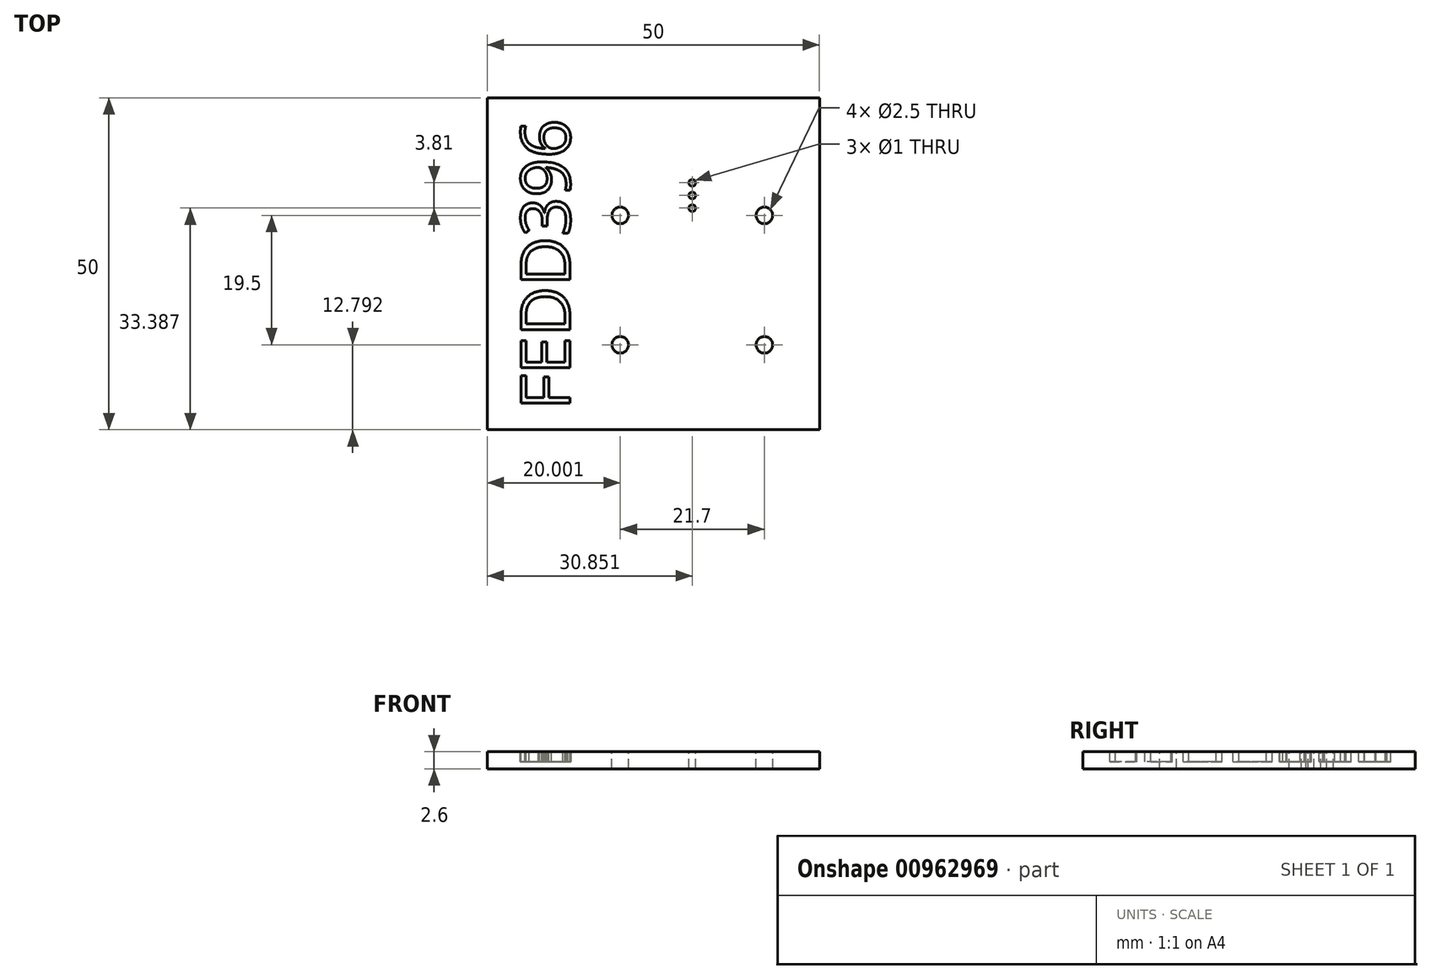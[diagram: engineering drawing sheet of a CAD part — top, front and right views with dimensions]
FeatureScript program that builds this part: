
annotation { "Feature Type Name" : "Feature", "Feature Type Description" : "" }
export const myFeature = defineFeature(function(context is Context, id is Id, definition is map)
    precondition{}
    {
        {
            var Q0;
            Q0=qCreatedBy(makeId("Top.planeOp"),FACE);
            var sketch = newSketch(context, id + "F0", { "sketchPlane" : qUnion([Q0])});
            skLineSegment(sketch, "E0.bottom", {"start": v(-43.16, 28.34) * mm, "end": v(6.84, 28.34) * mm});
            skLineSegment(sketch, "E0.top", {"start": v(-43.16, -21.66) * mm, "end": v(6.84, -21.66) * mm});
            skLineSegment(sketch, "E0.left", {"start": v(-43.16, 28.34) * mm, "end": v(-43.16, -21.66) * mm});
            skLineSegment(sketch, "E0.right", {"start": v(6.84, 28.34) * mm, "end": v(6.84, -21.66) * mm});
            skSolve(sketch);
        }
        {
            var Q0;
            Q0=makeQuery(id+"F0.imprint","IMPRINT",FACE,{"disambiguationData":[TD([[makeQuery(id+"F0.imprint","IMPRINT",EDGE,{"derivedFrom":sQuery(id+"F0.wireOp",EDGE,"E0.bottom")}),-1.0]])]});
            extrude(context, id + "F1", {"entities" : qUnion([Q0]), "depth" : 2.6 * mm, "offsetDistance" : 25 * mm});
        }
        {
            var Q0;
            Q0=makeQuery(id+"F1.opExtrude","CAP_FACE",FACE,{"disambiguationData":[OSD([sQuery(id+"F0.wireOp",EDGE,"E0.bottom"),sQuery(id+"F0.wireOp",EDGE,"E0.top"),sQuery(id+"F0.wireOp",EDGE,"E0.left"),sQuery(id+"F0.wireOp",EDGE,"E0.right")])],"isStart":false});
            var sketch = newSketch(context, id + "F2", { "sketchPlane" : qUnion([Q0])});
            skText(sketch, "E1", { "text": "FEDD396", "fontName": "OpenSans-Regular.ttf"});
            const initialGuessF2  = {"E1": [-0.03072, -0.01866, 0, 1, 0.00743]};
            skSetInitialGuess(sketch, initialGuessF2);
            skSolve(sketch);
        }
        {
            var Q0;
            Q0=qSketchRegion(id+"F2",true);
            extrude(context, id + "F3", {"entities" : qUnion([Q0]), "operationType" : NewBodyOperationType.REMOVE, "oppositeDirection" : true, "depth" : 1.5 * mm, "offsetDistance" : 25 * mm});
        }
        {
            var Q0;
            {var subQ0=sQuery(id+"F0.wireOp",EDGE,"E0.left");var subQ1=sQuery(id+"F0.wireOp",EDGE,"E0.bottom");var subQ2=sQuery(id+"F0.wireOp",EDGE,"E0.right");var subQ3=sQuery(id+"F0.wireOp",EDGE,"E0.top");Q0=makeQuery(id+"F3.boolean.opBoolean","SPLIT",FACE,{"disambiguationData":[TD([makeQuery(id+"F1.opExtrude","SWEPT_FACE",FACE,{"disambiguationData":[OSD([subQ1])]})])],"derivedFrom":makeQuery(id+"F1.opExtrude","CAP_FACE",FACE,{"disambiguationData":[OSD([subQ1,subQ3,subQ0,subQ2])],"isStart":false})});}
            var sketch = newSketch(context, id + "F4", { "sketchPlane" : qUnion([Q0])});
            skCircle(sketch, "E2", {"center": v(-23.16, -8.87) * mm, "radius": 1.25 * mm});
            skCircle(sketch, "E3", {"center": v(-23.16, 10.63) * mm, "radius": 1.25 * mm});
            skCircle(sketch, "E4", {"center": v(-12.3, 11.73) * mm, "radius": 0.5 * mm});
            skCircle(sketch, "E5", {"center": v(-12.3, 13.63) * mm, "radius": 0.5 * mm});
            skCircle(sketch, "E6", {"center": v(-12.3, 15.54) * mm, "radius": 0.5 * mm});
            skCircle(sketch, "E7", {"center": v(-1.46, -8.87) * mm, "radius": 1.25 * mm});
            skCircle(sketch, "E8", {"center": v(-1.46, 10.63) * mm, "radius": 1.25 * mm});
            skSolve(sketch);
        }
        {
            var Q0;
            Q0 = qSketchRegion(id + "F4", true);
            extrude(context, id + "F5", {"entities" : qUnion([Q0]), "operationType" : NewBodyOperationType.REMOVE, "endBound" : BoundingType.UP_TO_NEXT, "oppositeDirection" : true, "depth" : 25 * mm, "offsetDistance" : 25 * mm});
        }
    });
